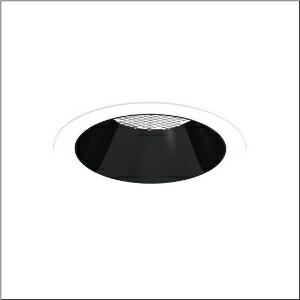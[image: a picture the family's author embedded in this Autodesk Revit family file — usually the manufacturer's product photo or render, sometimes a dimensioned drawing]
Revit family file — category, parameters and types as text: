
# Revit family: lunis_21_xl_51db17tf91c
name_source: partatom
category: Lighting Fixtures
units: mm (PartAtom-declared; Revit-internal decimal feet)

## family parameters
Cut with Voids When Loaded = No
Host = Face
Light Source = No
Part Type = Normal
Room Calculation Point = No
Round Connector Dimension = Use Diameter
Shared = No

## types (1)
- --- (1 x LED 3000 K ... 6500 K, 3510 lm, 25.4 W, 4000K)
    Apparent Load = 25 VA
    CIE Flux Codes = 92 100 100 100 100
    Color Rendering = 80
    Color Temperature = 4000K
    Default Elevation = 1800 mm
    Description = Lunis 21,  XL, downlight, light control with lens, of PMMA, anti glare with reflector, of aluminium, light emission: direct distribution, LED rated luminous flux: 3.510lm, light colour: 8tw, with terminal, 5-pole, mains connection: 220..240V, AC/DC, 0/50..60Hz, housing, round, of diecast aluminium, traffic white (RAL 9016), diameter: 230mm, clamping range: 1..40mm, protection rating (complete): IP20, protection rating (on room side): IP54, insulation class (complete): insulation class II (safety insulation), certification: CE, impact resistance: IK03, packaging unit: 1 piece
    Height = 0 mm  [stored 0 ft]
    Lamp = 1 x LED 3000 K ... 6500 K
    Lamp Light Flux = 3510 lm
    Lamp Power = 25.4 W
    Lamp count = 1
    Length = 230 mm
    Luminous efficacy = 138 lm/W
    Manufacturer = Siteco
    ModVariant = No
    Model = 51DB17TF91C
    Mounting Place = Ceiling
    Mounting Type = Recessed
    Number of Poles = 1
    OnlyDefault = Yes
    Power Factor = 1
    Product Name = Lunis 21 XL
    Product group = downlight
    ProductGroupID = 400
    Protection Class = Protection class II
    Protection Degree = IP 20
    RLX_Detail_Level = 1
    RLX_Emergency_Light_Flux = 0 lm
    RLX_Emergency_Type = 0
    RLX_Emergency_Type_DB = No
    RlxData = <blob elided: 19221 chars, md5=67c78ab9>
    Socket = socket
    Standby Power = 0 W
    System Light Flux = 3510 lm
    System Power = 25 W
    Type Comments = individual setting: CCT=4000K, colour temperature 4000K, luminous flux: 100 % | (ON | ON | OFF | OFF) | 700 mA
    Type Image = l_1291161.jpg
    URL = http://relux.com
    VarID = @adj_019724
    Voltage = 0 V
    Weight = 0.00 kg
    Width = 0 mm  [stored 0 ft]

note: [stored X ft] marks values corroborated as IEEE doubles in the binary element streams (Revit-internal decimal feet)

## geometry (parser evidence)
native form markers: Blend x4, Sweep x9
no freeform markers — native parametric forms only
